# Revit family: Window-Double_Hung-Andersen-400_Series-Tilt_Wash30410
name_source: partatom
category: Windows
revit_build: Autodesk Revit LT 2017 (Build: 20160225_1515(x64)
units: mm (PartAtom-declared; Revit-internal decimal feet)

## family parameters
Always vertical = Yes
Cut with Voids When Loaded = No
Host = Wall
OmniClass Number = 23.30.20.17.17.11
OmniClass Title = Single-Hung Windows
Room Calculation Point = No
Shared = No

## types (3) — shared parameters
. . Bottom Sash Lights High = 2
. . Lights Wide = 3
. . Top Sash Lights High = 2
..Exterior Trim Number 0 = No Exterior Trim
..Exterior Trim Number 1 = Brick Mould
..Exterior Trim Number 2 = 3 1/2'' Flat Casing
..Exterior Trim Number 3 = 4 1/2'' Flat Casing
..Pattern Number 1 = Colonial
..Pattern Number 2 = Colonial Top Sash Only
..Pattern Number 3 = Prairie Each Sash
..Pattern Number 4 = Prairie Top Sash Only
..Pattern Number 5 = Short Fractional
..Style Number 1 = Double Hung
..Style Number 2 = Double Hung Cottage
..Style Number 3 = Double Hung Reverse Cottage
Analytic Construction = <None>
Assembly Code = B2020100
Available Grille Bar Sizes = 3/4'', 7/8'', 1 1/8'', 2 1/4''
BS H Bars = 2
BS HGB DLO = 0' - 4"
BS M H = No
BS M V = Yes
BS S H = Yes
BS S V = No
Bar Center Line = 2
Between Glass Grille Bar Sizes = 3/4'', 1''
Description = Vinyl-clad hung window
Designation = TW
Enter Pattern Number = 1
Enter Style Number = 1
Extension Jamb = Yes
Exterior Grille Bar = Yes
Exterior Trim Finish = Fibrex Composite - Andersen - White
Exterior Unit Finish = Vinyl - Andersen - White
Family Version = 06.01.14
Fractional Lights High = 3
Fractional Lights Wide = 3
Glazing Material = Glass ‐ Andersen - Low-E4 SmartSun
HGO = 0' - 2 1/4"
Heat Transfer Coefficient (U) = 0.3 BTU/(h·ft²·°F)
Horizontal Craftsman Bar Size = 0' - 0 3/4"
Interior Casing Size = 0' - 2 1/4"
Interior Material = Wood - Andersen - Pine
JGO = 0' - 3 5/16"
LWide = 3
Learn About These Parameters = http://www.andersenwindows.com
Manufacturer = Andersen Corporation
Masonry Opening Offset = 0' - 0 1/4"
Model = 400-Series Tilt-Wash Double Hung
Product Documentation Link = http://www.andersenwindows.com
Product data url = https://bimobject.com
Rough Opening Offset = 0' - 0 1/4"
SGO = 0' - 4 1/2"
Solar Heat Gain Coefficient = 0.21
TFL = 1
TS H Bars = 2
TS HGB DLO = 0' - 4"
TS M H = No
TS M V = Yes
TS S H = Yes
TS S H Craftsman = No
TS S V = No
Thermal Resistance (R) = 3.3300 (h·ft²·°F)/BTU
Type Comments = Vinyl-clad double hung window
URL = www.andersenwindows.com
V Bars = 2
Visual Light Transmittance = 0.48
Wall Closure = By host
casing1 = 0' - 0 1/4"
casing2 = 0' - 0 7/8"
casing3 = 0' - 0 1/2"
casing4 = 0' - 4 1/4"
casingS1 = 0' - 0 3/16"
casingS2 = 0' - 0 3/16"
sill nose 2 = 0' - 1 15/16"
sill nose1 = 0' - 1 13/16"
zero-valued in all types: TFB

## per-type parameters (varying)
- Window-Double_Hung-Andersen-400_Series-Tilt_Wash: BS SH DLO=1' - 5 7/16"; BS V DLO=2' - 1 7/8"; Between Glass Grille Bar=Yes; Between Glass Grille Bar Finish=Stainless Steel - Andersen - Standard; Casing Visibility=No; Check Rail Location=2' - 1 7/8"; Default Sill Height=1' - 10"; Enter Exterior Trim Number=0; Grille Bar Size=0' - 0 7/8"; H DLO=2' - 5 3/8"; Head MO Offset=0' - 0 1/4"; Height=5' - 0"; Interior Casing=Yes; Interior Grille Bar=Yes; Masonry Height=5' - 0 1/2"; Masonry Width=3' - 0 1/2"; Nail Fin Visibility=Yes; Rough Height=5' - 0 1/2"; Rough Width=3' - 0 1/2"; Sill MO Offset=0' - 0 1/4"; TS SH DLO=1' - 3 3/16"; TS V Bar Length=2' - 1 7/8"; TS V DLO=2' - 1 7/8"; VGB DLO=0' - 9 7/32"; Void Offset 1=0' - 0"; Void Offset 2=0' - 0"; Width=3' - 0"
- Window-Double_Hung-Andersen-400_Series-Tilt_Wash 2646: BS SH DLO=1' - 3 15/16"; BS V DLO=1' - 10 7/8"; Between Glass Grille Bar=No; Between Glass Grille Bar Finish=Stainless Steel - Andersen - Standard; Casing Visibility=Yes; Check Rail Location=1' - 10 7/8"; Default Sill Height=2' - 4"; Enter Exterior Trim Number=3; Grille Bar Size=0' - 0 7/8"; H DLO=1' - 11 3/8"; Head MO Offset=0' - 4 1/2"; Height=4' - 6"; Interior Casing=No; Interior Grille Bar=No; Masonry Height=5' - 0 11/16"; Masonry Width=3' - 3"; Nail Fin Visibility=No; Rough Height=4' - 6 1/2"; Rough Width=2' - 6 1/2"; Sill MO Offset=0' - 2 3/16"; TS SH DLO=1' - 1 11/16"; TS V Bar Length=1' - 10 7/8"; TS V DLO=1' - 10 7/8"; VGB DLO=0' - 7 7/32"; Void Offset 1=0' - 4 1/4"; Void Offset 2=0' - 1 15/16"; Width=2' - 6"
- Window-Double_Hung-Andersen-400_Series-Tilt_Wash 30410: BS SH DLO=1' - 5 7/16"; BS V DLO=2' - 1 7/8"; Between Glass Grille Bar=No; Between Glass Grille Bar Finish=Fibrex Composite - Andersen - White; Casing Visibility=Yes; Check Rail Location=2' - 1 7/8"; Default Sill Height=1' - 10"; Enter Exterior Trim Number=3; Grille Bar Size=0' - 1 1/8"; H DLO=2' - 5 3/8"; Head MO Offset=0' - 4 1/2"; Height=5' - 0"; Interior Casing=No; Interior Grille Bar=No; Masonry Height=5' - 6 11/16"; Masonry Width=3' - 9"; Nail Fin Visibility=No; Rough Height=5' - 0 1/2"; Rough Width=3' - 0 1/2"; Sill MO Offset=0' - 2 3/16"; TS SH DLO=1' - 3 3/16"; TS V Bar Length=2' - 1 7/8"; TS V DLO=2' - 1 7/8"; VGB DLO=0' - 9 1/32"; Void Offset 1=0' - 4 1/4"; Void Offset 2=0' - 1 15/16"; Width=3' - 0"

## geometry (parser evidence)
native form markers: Blend x16, Sweep x6
no freeform markers — native parametric forms only
